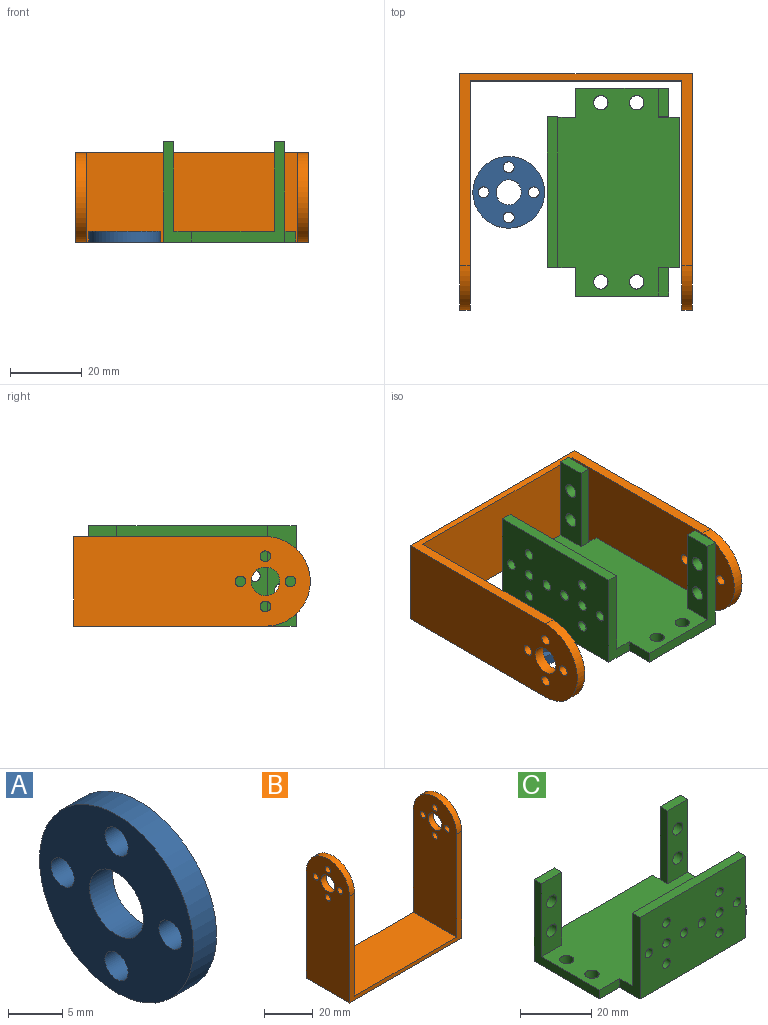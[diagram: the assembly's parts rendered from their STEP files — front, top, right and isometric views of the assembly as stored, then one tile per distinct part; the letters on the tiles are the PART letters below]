
ASSEMBLY  parts=3 mates=2
PART A: 8 faces, bbox 3x20x20 mm
  f0: cylinder r=1.5mm len=3mm, axis (-1,0,0), area 28.3mm2, adj f5,f6
  f1: cylinder r=1.5mm len=3mm, axis (-1,0,0), area 28.3mm2, adj f5,f6
  f2: cylinder r=1.5mm len=3mm, axis (-1,0,0), area 28.3mm2, adj f5,f6
  f3: cylinder r=1.5mm len=3mm, axis (-1,0,0), area 28.3mm2, adj f5,f6
  f4: cylinder r=10mm len=20mm, axis (-1,0,0), area 188.5mm2, adj f5,f6
  f5: plane 20x20mm, normal (1,0,0), area 247.4mm2, adj f0,f1,f2,f3,f4,f7
  f6: plane 20x20mm, normal (-1,0,0), area 247.4mm2, adj f0,f1,f2,f3,f4,f7
  f7: cylinder r=3.5mm len=7mm, axis (1,0,0), area 66mm2, adj f5,f6
PART B: 20 faces, bbox 65x25x66 mm
  f0: plane 66x25mm, normal (-1,0,0), area 1504.4mm2, adj f5,f6,f7,f9,f15,f16,f17,f18
  f1: plane 66x25mm, normal (1,0,0), area 1504.4mm2, adj f5,f6,f7,f8,f10,f11,f12,f13
  f2: plane 64x25mm, normal (1,0,0), area 1454.4mm2, adj f4,f5,f6,f9,f15,f16,f17,f18
  f3: plane 64x25mm, normal (-1,0,0), area 1454.4mm2, adj f4,f5,f6,f8,f10,f11,f12,f13
  f4: plane 59x25mm, normal (0,0,1), area 1475mm2, adj f2,f3,f5,f6
  f5: plane 65x53.5mm, normal (0,-1,0), area 439mm2, adj f0,f1,f2,f3,f4,f7,f8,f9
  f6: plane 65x53.5mm, normal (0,1,0), area 439mm2, adj f0,f1,f2,f3,f4,f7,f8,f9
  f7: plane 65x25mm, normal (0,0,-1), area 1625mm2, adj f0,f1,f5,f6
  f8: cylinder r=12.5mm len=25mm, axis (-1,0,0), area 117.8mm2, adj f1,f3,f5,f6
  f9: cylinder r=12.5mm len=25mm, axis (-1,0,0), area 117.8mm2, adj f0,f2,f5,f6
  f10: cylinder r=1.5mm len=3mm, axis (-1,0,0), area 28.3mm2, adj f1,f3
  f11: cylinder r=1.5mm len=3mm, axis (-1,0,0), area 28.3mm2, adj f1,f3
  f12: cylinder r=4mm len=8mm, axis (-1,0,0), area 75.4mm2, adj f1,f3
  f13: cylinder r=1.5mm len=3mm, axis (-1,0,0), area 28.3mm2, adj f1,f3
  f14: cylinder r=1.5mm len=3mm, axis (-1,0,0), area 28.3mm2, adj f1,f3
  f15: cylinder r=1.5mm len=3mm, axis (-1,0,0), area 28.3mm2, adj f0,f2
  f16: cylinder r=1.5mm len=3mm, axis (-1,0,0), area 28.3mm2, adj f0,f2
  f17: cylinder r=4mm len=8mm, axis (-1,0,0), area 75.4mm2, adj f0,f2
  f18: cylinder r=1.5mm len=3mm, axis (-1,0,0), area 28.3mm2, adj f0,f2
  f19: cylinder r=1.5mm len=3mm, axis (-1,0,0), area 28.3mm2, adj f0,f2
PART C: 40 faces, bbox 58x37x28 mm
  f0: plane 58x34mm, normal (0,0,1), area 1745.7mm2, adj f1,f2,f3,f5,f6,f7,f9,f10
  f1: plane 28x26mm, normal (-1,0,0), area 153mm2, adj f0,f2,f12,f13,f16,f18
  f2: plane 8x3mm, normal (0,-1,0), area 24mm2, adj f0,f1,f3,f13
  f3: plane 28x8mm, normal (-1,0,0), area 99mm2, adj f0,f2,f4,f13,f14,f15
  f4: plane 42x28mm, normal (0,-1,0), area 1105.3mm2, adj f3,f5,f13,f15,f26,f27,f28,f29
  f5: plane 28x8mm, normal (1,0,0), area 99mm2, adj f0,f4,f6,f13,f14,f15
  f6: plane 8x3mm, normal (0,-1,0), area 24mm2, adj f0,f5,f7,f13
  f7: plane 28x26mm, normal (1,0,0), area 153mm2, adj f0,f6,f8,f13,f19,f21
  f8: plane 28x8mm, normal (0,1,0), area 198.9mm2, adj f7,f9,f13,f20,f21,f22,f23
  f9: plane 3x3mm, normal (1,0,0), area 9mm2, adj f0,f8,f10,f13
  f10: plane 42x3mm, normal (0,1,0), area 126mm2, adj f0,f9,f11,f13
  f11: plane 3x3mm, normal (-1,0,0), area 9mm2, adj f0,f10,f12,f13
  f12: plane 28x8mm, normal (0,1,0), area 198.9mm2, adj f1,f11,f13,f17,f18,f24,f25
  f13: plane 58x37mm, normal (0,0,-1), area 1919.7mm2, adj f1,f2,f3,f4,f5,f6,f7,f8
  f14: plane 42x25mm, normal (0,1,0), area 979.3mm2, adj f0,f3,f5,f15,f26,f27,f28,f29
  f15: plane 42x3mm, normal (0,0,1), area 126mm2, adj f3,f4,f5,f14
  f16: plane 25x8mm, normal (0,-1,0), area 174.9mm2, adj f0,f1,f17,f18,f24,f25
  f17: plane 25x3mm, normal (1,0,0), area 75mm2, adj f0,f12,f16,f18
  f18: plane 8x3mm, normal (0,0,1), area 24mm2, adj f1,f12,f16,f17
  f19: plane 25x8mm, normal (0,-1,0), area 174.9mm2, adj f0,f7,f20,f21,f22,f23
  f20: plane 25x3mm, normal (-1,0,0), area 75mm2, adj f0,f8,f19,f21
  f21: plane 8x3mm, normal (0,0,1), area 24mm2, adj f7,f8,f19,f20
  f22: cylinder r=2mm len=4mm, axis (0,-1,0), area 37.7mm2, adj f8,f19
  f23: cylinder r=2mm len=4mm, axis (0,-1,0), area 37.7mm2, adj f8,f19
  f24: cylinder r=2mm len=4mm, axis (0,-1,0), area 37.7mm2, adj f12,f16
  f25: cylinder r=2mm len=4mm, axis (0,-1,0), area 37.7mm2, adj f12,f16
  f26: cylinder r=1.5mm len=3mm, axis (0,-1,0), area 28.3mm2, adj f4,f14
  f27: cylinder r=1.5mm len=3mm, axis (0,-1,0), area 28.3mm2, adj f4,f14
  f28: cylinder r=1.5mm len=3mm, axis (0,-1,0), area 28.3mm2, adj f4,f14
  f29: cylinder r=1.5mm len=3mm, axis (0,-1,0), area 28.3mm2, adj f4,f14
  f30: cylinder r=1.5mm len=3mm, axis (0,-1,0), area 28.3mm2, adj f4,f14
  f31: cylinder r=1.5mm len=3mm, axis (0,-1,0), area 28.3mm2, adj f4,f14
  f32: cylinder r=1.5mm len=3mm, axis (0,-1,0), area 28.3mm2, adj f4,f14
  f33: cylinder r=1.5mm len=3mm, axis (0,-1,0), area 28.3mm2, adj f4,f14
  f34: cylinder r=1.5mm len=3mm, axis (0,-1,0), area 28.3mm2, adj f4,f14
  f35: cylinder r=1.5mm len=3mm, axis (0,-1,0), area 28.3mm2, adj f4,f14
  f36: cylinder r=2mm len=4mm, axis (0,0,-1), area 37.7mm2, adj f0,f13
  f37: cylinder r=2mm len=4mm, axis (0,0,-1), area 37.7mm2, adj f0,f13
  f38: cylinder r=2mm len=4mm, axis (0,0,-1), area 37.7mm2, adj f0,f13
  f39: cylinder r=2mm len=4mm, axis (0,0,-1), area 37.7mm2, adj f0,f13
PLACE A rot(axis=(0,-1,0),90deg) t=(-18.77,4.61,38.51)mm
PLACE B rot(axis=(1,0,0),90deg) t=(-32.5,37.66,38.51)mm
PLACE C rot(axis=(0,0,-1),90deg) t=(-8.07,33.61,38.51)mm
MATE planar A.f4 <-> C.f13  axis (0,0,-1) through (-18.77,4.61,38.51)mm
MATE planar C.f13 <-> B.f5  axis (0,0,-1) through (10.93,4.61,38.51)mm
